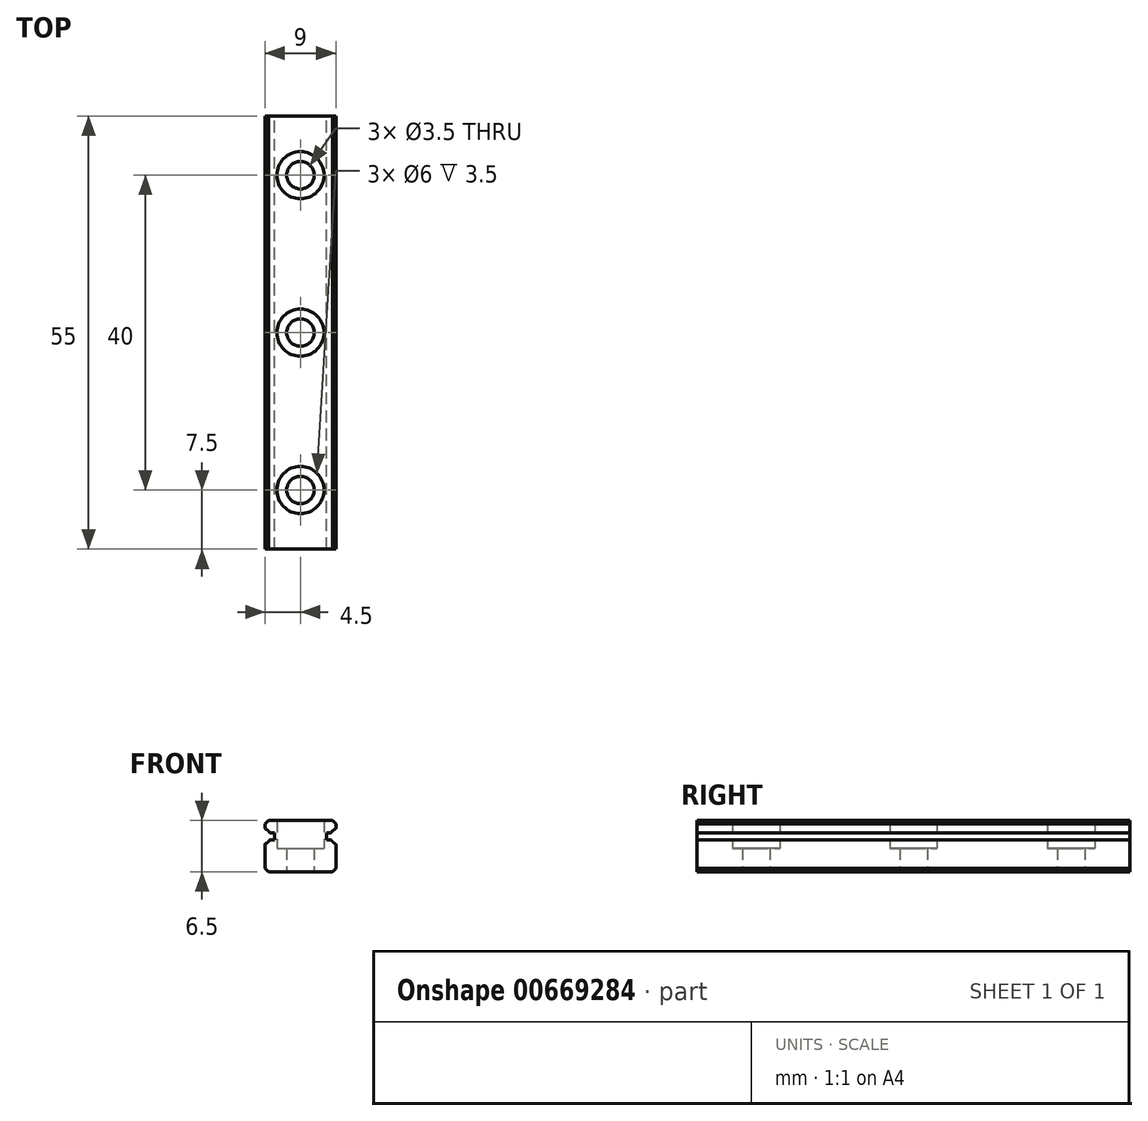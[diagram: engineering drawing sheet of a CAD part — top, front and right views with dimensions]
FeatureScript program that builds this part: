
annotation { "Feature Type Name" : "Feature", "Feature Type Description" : "" }
export const myFeature = defineFeature(function(context is Context, id is Id, definition is map)
    precondition{}
    {
        {
            var Q0;
            Q0=qCreatedBy(makeId("Front.planeOp"),FACE);
            var sketch = newSketch(context, id + "F0", { "sketchPlane" : qUnion([Q0])});
            skPoint(sketch, "E0.middle", {"position": v(0, 0) * mm});
            skLineSegment(sketch, "E1.bottom", {"start": v(0, -3.25) * mm, "end": v(-4.08, -3.25) * mm});
            skLineSegment(sketch, "E1.top", {"start": v(0, 3.25) * mm, "end": v(-4.08, 3.25) * mm});
            skLineSegment(sketch, "E1.right", {"start": v(-4.5, -2.83) * mm, "end": v(-4.5, 0.16) * mm});
            skArc(sketch, "E2", {"start": v(-4.38, 0.34) * mm, "mid": v(-4.15, 0.5) * mm, "end": v(-3.96, 0.7) * mm});
            skLineSegment(sketch, "E3", {"start": v(-3.3, 0.8) * mm, "end": v(-3.8, 0.8) * mm});
            skLineSegment(sketch, "E4", {"start": v(-3.3, 1.7) * mm, "end": v(-3.8, 1.7) * mm});
            skLineSegment(sketch, "E5", {"start": v(-4.5, 2.83) * mm, "end": v(-4.08, 3.25) * mm});
            skLineSegment(sketch, "E6.MirrorCS", {"start": v(-4.5, -2.83) * mm, "end": v(-4.08, -3.25) * mm});
            skPoint(sketch, "E7.orphan", {"position": v(-4.5, 3.25) * mm});
            skLineSegment(sketch, "E8.trimOffspring", {"start": v(-4.5, 2.34) * mm, "end": v(-4.5, 2.83) * mm});
            skArc(sketch, "E9.trimOffspring", {"start": v(-3.96, 1.8) * mm, "mid": v(-4.15, 2) * mm, "end": v(-4.38, 2.16) * mm});
            skPoint(sketch, "E10.orphan", {"position": v(-4.5, -3.25) * mm});
            skLineSegment(sketch, "E11", {"start": v(-3.3, 1.7) * mm, "end": v(-3.3, 0.8) * mm});
            skLineSegment(sketch, "E12", {"start": v(-4.8, 1.25) * mm, "end": v(0, 1.25) * mm, "construction": true});
            skLineSegment(sketch, "E13", {"start": v(0, 3.25) * mm, "end": v(0, -3.25) * mm, "construction": true});
            skPoint(sketch, "E14.0.visualSharp", {"position": v(-4.5, 0.3) * mm});
            skArc(sketch, "E14.0.filletArc", {"start": v(-4.38, 0.34) * mm, "mid": v(-4.47, 0.27) * mm, "end": v(-4.5, 0.16) * mm});
            skPoint(sketch, "E14.1.visualSharp", {"position": v(-3.9, 0.8) * mm});
            skArc(sketch, "E14.1.filletArc", {"start": v(-3.8, 0.8) * mm, "mid": v(-3.89, 0.78) * mm, "end": v(-3.96, 0.7) * mm});
            skPoint(sketch, "E14.2.visualSharp", {"position": v(-3.9, 1.7) * mm});
            skArc(sketch, "E14.2.filletArc", {"start": v(-3.96, 1.8) * mm, "mid": v(-3.89, 1.72) * mm, "end": v(-3.8, 1.7) * mm});
            skPoint(sketch, "E14.3.visualSharp", {"position": v(-4.5, 2.2) * mm});
            skArc(sketch, "E14.3.filletArc", {"start": v(-4.5, 2.34) * mm, "mid": v(-4.47, 2.23) * mm, "end": v(-4.38, 2.16) * mm});
            skLineSegment(sketch, "E15.MirrorCS", {"start": v(0, 3.25) * mm, "end": v(4.08, 3.25) * mm});
            skLineSegment(sketch, "E16.MirrorCS", {"start": v(4.5, 2.83) * mm, "end": v(4.08, 3.25) * mm});
            skLineSegment(sketch, "E17.MirrorCS", {"start": v(4.5, 2.34) * mm, "end": v(4.5, 2.83) * mm});
            skArc(sketch, "E18.MirrorCS", {"start": v(4.5, 2.34) * mm, "mid": v(4.47, 2.23) * mm, "end": v(4.38, 2.16) * mm});
            skArc(sketch, "E19.MirrorCS", {"start": v(3.96, 1.8) * mm, "mid": v(4.15, 2) * mm, "end": v(4.38, 2.16) * mm});
            skArc(sketch, "E20.MirrorCS", {"start": v(3.96, 1.8) * mm, "mid": v(3.89, 1.72) * mm, "end": v(3.8, 1.7) * mm});
            skLineSegment(sketch, "E21.MirrorCS", {"start": v(3.3, 1.7) * mm, "end": v(3.8, 1.7) * mm});
            skLineSegment(sketch, "E22.MirrorCS", {"start": v(3.3, 1.7) * mm, "end": v(3.3, 0.8) * mm});
            skLineSegment(sketch, "E23.MirrorCS", {"start": v(3.3, 0.8) * mm, "end": v(3.8, 0.8) * mm});
            skArc(sketch, "E24.MirrorCS", {"start": v(3.8, 0.8) * mm, "mid": v(3.89, 0.78) * mm, "end": v(3.96, 0.7) * mm});
            skArc(sketch, "E25.MirrorCS", {"start": v(4.38, 0.34) * mm, "mid": v(4.15, 0.5) * mm, "end": v(3.96, 0.7) * mm});
            skArc(sketch, "E26.MirrorCS", {"start": v(4.38, 0.34) * mm, "mid": v(4.47, 0.27) * mm, "end": v(4.5, 0.16) * mm});
            skLineSegment(sketch, "E27.MirrorCS", {"start": v(4.5, -2.83) * mm, "end": v(4.5, 0.16) * mm});
            skLineSegment(sketch, "E28.MirrorCS", {"start": v(4.5, -2.83) * mm, "end": v(4.08, -3.25) * mm});
            skLineSegment(sketch, "E29.MirrorCS", {"start": v(0, -3.25) * mm, "end": v(4.08, -3.25) * mm});
            skSolve(sketch);
        }
        {
            var Q0;
            Q0=makeQuery(id+"F0.imprint","IMPRINT",FACE,{"disambiguationData":[TD([[makeQuery(id+"F0.imprint","IMPRINT",EDGE,{"derivedFrom":sQuery(id+"F0.wireOp",EDGE,"E1.bottom")}),-1.0]])]});
            extrude(context, id + "F1", {"entities" : qUnion([Q0]), "depth" : 55 * mm, "offsetDistance" : 25 * mm});
        }
        {
            var Q0;
            Q0=makeQuery(id+"F1.opExtrude","SWEPT_FACE",FACE,{"disambiguationData":[OSD([sQuery(id+"F0.wireOp",EDGE,"E1.top")])]});
            var sketch = newSketch(context, id + "F2", { "sketchPlane" : qUnion([Q0])});
            skPoint(sketch, "E30", {"position": v(0, -7.5) * mm});
            skPoint(sketch, "E31.1.0.0", {"position": v(0, -27.5) * mm});
            skPoint(sketch, "E31.2.0.0", {"position": v(0, -47.5) * mm});
            skPoint(sketch, "E31.3.0.0", {"position": v(0, -67.5) * mm});
            skPoint(sketch, "E31.4.0.0", {"position": v(0, -87.5) * mm});
            skPoint(sketch, "E31.5.0.0", {"position": v(0, -107.5) * mm});
            skPoint(sketch, "E31.6.0.0", {"position": v(0, -127.5) * mm});
            skPoint(sketch, "E31.7.0.0", {"position": v(0, -147.5) * mm});
            skPoint(sketch, "E31.8.0.0", {"position": v(0, -167.5) * mm});
            skPoint(sketch, "E31.9.0.0", {"position": v(0, -187.5) * mm});
            skPoint(sketch, "E31.10.0.0", {"position": v(0, -207.5) * mm});
            skPoint(sketch, "E31.11.0.0", {"position": v(0, -227.5) * mm});
            skPoint(sketch, "E31.12.0.0", {"position": v(0, -247.5) * mm});
            skPoint(sketch, "E31.13.0.0", {"position": v(0, -267.5) * mm});
            skPoint(sketch, "E31.14.0.0", {"position": v(0, -287.5) * mm});
            skPoint(sketch, "E31.15.0.0", {"position": v(0, -307.5) * mm});
            skPoint(sketch, "E31.16.0.0", {"position": v(0, -327.5) * mm});
            skPoint(sketch, "E31.17.0.0", {"position": v(0, -347.5) * mm});
            skPoint(sketch, "E31.18.0.0", {"position": v(0, -367.5) * mm});
            skPoint(sketch, "E31.19.0.0", {"position": v(0, -387.5) * mm});
            skPoint(sketch, "E31.20.0.0", {"position": v(0, -407.5) * mm});
            skPoint(sketch, "E31.21.0.0", {"position": v(0, -427.5) * mm});
            skPoint(sketch, "E31.22.0.0", {"position": v(0, -447.5) * mm});
            skPoint(sketch, "E31.23.0.0", {"position": v(0, -467.5) * mm});
            skPoint(sketch, "E31.24.0.0", {"position": v(0, -487.5) * mm});
            skPoint(sketch, "E31.25.0.0", {"position": v(0, -507.5) * mm});
            skPoint(sketch, "E31.26.0.0", {"position": v(0, -527.5) * mm});
            skPoint(sketch, "E31.27.0.0", {"position": v(0, -547.5) * mm});
            skPoint(sketch, "E31.28.0.0", {"position": v(0, -567.5) * mm});
            skPoint(sketch, "E31.29.0.0", {"position": v(0, -587.5) * mm});
            skLineSegment(sketch, "E31.direction1", {"start": v(0, -7.5) * mm, "end": v(0, -27.5) * mm, "construction": true});
            skPoint(sketch, "E32.0.30.0", {"position": v(0, -607.5) * mm});
            skPoint(sketch, "E32.0.31.0", {"position": v(0, -627.5) * mm});
            skPoint(sketch, "E32.0.32.0", {"position": v(0, -647.5) * mm});
            skPoint(sketch, "E32.0.33.0", {"position": v(0, -667.5) * mm});
            skPoint(sketch, "E32.0.34.0", {"position": v(0, -687.5) * mm});
            skPoint(sketch, "E32.0.35.0", {"position": v(0, -707.5) * mm});
            skPoint(sketch, "E32.0.36.0", {"position": v(0, -727.5) * mm});
            skPoint(sketch, "E32.0.37.0", {"position": v(0, -747.5) * mm});
            skPoint(sketch, "E32.0.38.0", {"position": v(0, -767.5) * mm});
            skPoint(sketch, "E32.0.39.0", {"position": v(0, -787.5) * mm});
            skPoint(sketch, "E33.0.40.0", {"position": v(0, -807.5) * mm});
            skPoint(sketch, "E33.0.41.0", {"position": v(0, -827.5) * mm});
            skPoint(sketch, "E33.0.42.0", {"position": v(0, -847.5) * mm});
            skPoint(sketch, "E33.0.43.0", {"position": v(0, -867.5) * mm});
            skPoint(sketch, "E33.0.44.0", {"position": v(0, -887.5) * mm});
            skPoint(sketch, "E33.0.45.0", {"position": v(0, -907.5) * mm});
            skPoint(sketch, "E33.0.46.0", {"position": v(0, -927.5) * mm});
            skPoint(sketch, "E33.0.47.0", {"position": v(0, -947.5) * mm});
            skPoint(sketch, "E33.0.48.0", {"position": v(0, -967.5) * mm});
            skPoint(sketch, "E33.0.49.0", {"position": v(0, -987.5) * mm});
            skPoint(sketch, "E34.0.50.0", {"position": v(0, -1007.5) * mm});
            skPoint(sketch, "E34.0.51.0", {"position": v(0, -1027.5) * mm});
            skPoint(sketch, "E34.0.52.0", {"position": v(0, -1047.5) * mm});
            skPoint(sketch, "E34.0.53.0", {"position": v(0, -1067.5) * mm});
            skPoint(sketch, "E34.0.54.0", {"position": v(0, -1087.5) * mm});
            skPoint(sketch, "E34.0.55.0", {"position": v(0, -1107.5) * mm});
            skPoint(sketch, "E34.0.56.0", {"position": v(0, -1127.5) * mm});
            skPoint(sketch, "E34.0.57.0", {"position": v(0, -1147.5) * mm});
            skPoint(sketch, "E34.0.58.0", {"position": v(0, -1167.5) * mm});
            skPoint(sketch, "E34.0.59.0", {"position": v(0, -1187.5) * mm});
            skSolve(sketch);
        }
        {
            var Q0;
            Q0=sQuery(id+"F2.wireOp",VERTEX,"E34.0.52.0");
            var Q1;
            Q1=sQuery(id+"F2.wireOp",VERTEX,"E30");
            var Q2;
            Q2=sQuery(id+"F2.wireOp",VERTEX,"E34.0.59.0");
            var Q3;
            Q3=sQuery(id+"F2.wireOp",VERTEX,"E31.25.0.0");
            var Q4;
            Q4=sQuery(id+"F2.wireOp",VERTEX,"E34.0.50.0");
            var Q5;
            Q5=sQuery(id+"F2.wireOp",VERTEX,"E31.3.0.0");
            var Q6;
            Q6=sQuery(id+"F2.wireOp",VERTEX,"E33.0.40.0");
            var Q7;
            Q7=sQuery(id+"F2.wireOp",VERTEX,"E32.0.30.0");
            var Q8;
            Q8=sQuery(id+"F2.wireOp",VERTEX,"E32.0.33.0");
            var Q9;
            Q9=sQuery(id+"F2.wireOp",VERTEX,"E31.direction1.end");
            var Q10;
            Q10=sQuery(id+"F2.wireOp",VERTEX,"E31.24.0.0");
            var Q11;
            Q11=sQuery(id+"F2.wireOp",VERTEX,"E31.9.0.0");
            var Q12;
            Q12=sQuery(id+"F2.wireOp",VERTEX,"E31.19.0.0");
            var Q13;
            Q13=sQuery(id+"F2.wireOp",VERTEX,"E31.23.0.0");
            var Q14;
            Q14=sQuery(id+"F2.wireOp",VERTEX,"E33.0.47.0");
            var Q15;
            Q15=sQuery(id+"F2.wireOp",VERTEX,"E31.4.0.0");
            var Q16;
            Q16=sQuery(id+"F2.wireOp",VERTEX,"E31.20.0.0");
            var Q17;
            Q17=sQuery(id+"F2.wireOp",VERTEX,"E31.11.0.0");
            var Q18;
            Q18=sQuery(id+"F2.wireOp",VERTEX,"E32.0.32.0");
            var Q19;
            Q19=sQuery(id+"F2.wireOp",VERTEX,"E32.0.39.0");
            var Q20;
            Q20=sQuery(id+"F2.wireOp",VERTEX,"E32.0.36.0");
            var Q21;
            Q21=sQuery(id+"F2.wireOp",VERTEX,"E32.0.37.0");
            var Q22;
            Q22=sQuery(id+"F2.wireOp",VERTEX,"E33.0.49.0");
            var Q23;
            Q23=sQuery(id+"F2.wireOp",VERTEX,"E32.0.38.0");
            var Q24;
            Q24=sQuery(id+"F2.wireOp",VERTEX,"E34.0.56.0");
            var Q25;
            Q25=sQuery(id+"F2.wireOp",VERTEX,"E33.0.44.0");
            var Q26;
            Q26=sQuery(id+"F2.wireOp",VERTEX,"E31.10.0.0");
            var Q27;
            Q27=sQuery(id+"F2.wireOp",VERTEX,"E31.28.0.0");
            var Q28;
            Q28=sQuery(id+"F2.wireOp",VERTEX,"E34.0.55.0");
            var Q29;
            Q29=sQuery(id+"F2.wireOp",VERTEX,"E32.0.35.0");
            var Q30;
            Q30=sQuery(id+"F2.wireOp",VERTEX,"E34.0.51.0");
            var Q31;
            Q31=sQuery(id+"F2.wireOp",VERTEX,"E31.13.0.0");
            var Q32;
            Q32=sQuery(id+"F2.wireOp",VERTEX,"E31.2.0.0");
            var Q33;
            Q33=sQuery(id+"F2.wireOp",VERTEX,"E31.21.0.0");
            var Q34;
            Q34=sQuery(id+"F2.wireOp",VERTEX,"E32.0.34.0");
            var Q35;
            Q35=sQuery(id+"F2.wireOp",VERTEX,"E31.16.0.0");
            var Q36;
            Q36=sQuery(id+"F2.wireOp",VERTEX,"E31.7.0.0");
            var Q37;
            Q37=sQuery(id+"F2.wireOp",VERTEX,"E32.0.31.0");
            var Q38;
            Q38=sQuery(id+"F2.wireOp",VERTEX,"E31.8.0.0");
            var Q39;
            Q39=sQuery(id+"F2.wireOp",VERTEX,"E34.0.57.0");
            var Q40;
            Q40=sQuery(id+"F2.wireOp",VERTEX,"E31.17.0.0");
            var Q41;
            Q41=sQuery(id+"F2.wireOp",VERTEX,"E31.12.0.0");
            var Q42;
            Q42=sQuery(id+"F2.wireOp",VERTEX,"E33.0.48.0");
            var Q43;
            Q43=sQuery(id+"F2.wireOp",VERTEX,"E31.18.0.0");
            var Q44;
            Q44=sQuery(id+"F2.wireOp",VERTEX,"E31.15.0.0");
            var Q45;
            Q45=sQuery(id+"F2.wireOp",VERTEX,"E34.0.54.0");
            var Q46;
            Q46=sQuery(id+"F2.wireOp",VERTEX,"E34.0.58.0");
            var Q47;
            Q47=sQuery(id+"F2.wireOp",VERTEX,"E33.0.46.0");
            var Q48;
            Q48=sQuery(id+"F2.wireOp",VERTEX,"E31.22.0.0");
            var Q49;
            Q49=sQuery(id+"F2.wireOp",VERTEX,"E31.14.0.0");
            var Q50;
            Q50=sQuery(id+"F2.wireOp",VERTEX,"E31.29.0.0");
            var Q51;
            Q51=sQuery(id+"F2.wireOp",VERTEX,"E33.0.45.0");
            var Q52;
            Q52=sQuery(id+"F2.wireOp",VERTEX,"E31.6.0.0");
            var Q53;
            Q53=sQuery(id+"F2.wireOp",VERTEX,"E33.0.42.0");
            var Q54;
            Q54=sQuery(id+"F2.wireOp",VERTEX,"E31.5.0.0");
            var Q55;
            Q55=sQuery(id+"F2.wireOp",VERTEX,"E31.26.0.0");
            var Q56;
            Q56=sQuery(id+"F2.wireOp",VERTEX,"E33.0.41.0");
            var Q57;
            Q57=sQuery(id+"F2.wireOp",VERTEX,"E34.0.53.0");
            var Q58;
            Q58=sQuery(id+"F2.wireOp",VERTEX,"E33.0.43.0");
            var Q59;
            Q59=sQuery(id+"F2.wireOp",VERTEX,"E31.27.0.0");
            var Q60;
            Q60=makeQuery(id+"F1.opExtrude","SWEPT_BODY",BODY,{"disambiguationData":[OSD([sQuery(id+"F0.wireOp",EDGE,"E1.bottom"),sQuery(id+"F0.wireOp",EDGE,"E1.top"),sQuery(id+"F0.wireOp",EDGE,"E1.left"),sQuery(id+"F0.wireOp",EDGE,"E1.right"),sQuery(id+"F0.wireOp",EDGE,"E2"),sQuery(id+"F0.wireOp",EDGE,"6b0fc32b-6b11-43fe-8143-8292133b5b09"),sQuery(id+"F0.wireOp",EDGE,"cceb31f5-90f8-4f8b-8e4c-378b10a37ca3"),sQuery(id+"F0.wireOp",EDGE,"a502a9f8-cd79-42af-b1f8-1e47760ff194"),sQuery(id+"F0.wireOp",EDGE,"E3"),sQuery(id+"F0.wireOp",EDGE,"E4"),sQuery(id+"F0.wireOp",EDGE,"E5"),sQuery(id+"F0.wireOp",EDGE,"f517c70c-7447-4023-b0b2-4cd41b919897.MirrorCS"),sQuery(id+"F0.wireOp",EDGE,"1ef16270-10e6-46b5-932e-9d39ff3028f5.MirrorCS"),sQuery(id+"F0.wireOp",EDGE,"E6.MirrorCS"),sQuery(id+"F0.wireOp",EDGE,"E8.trimOffspring"),sQuery(id+"F0.wireOp",EDGE,"E9.trimOffspring"),sQuery(id+"F0.wireOp",EDGE,"67894982-00cf-4a8e-9807-128cd8b838d2.trimOffspring"),sQuery(id+"F0.wireOp",EDGE,"f8798748-f2cf-45fa-b449-962a41418a19.trimOffspring"),sQuery(id+"F0.wireOp",EDGE,"E11"),sQuery(id+"F0.wireOp",EDGE,"PUignqLn-Sdhw-Ye5u-4mVw-quTeRiMXk1mG")])]});
            hole(context, id + "F3", {"style" : HoleStyle.C_BORE, "endStyle" : HoleEndStyle.THROUGH, "holeDiameter" : 3.5 * mm, "cBoreDiameter" : 6 * mm, "cBoreDepth" : 3.5 * mm, "majorDiameter" : 5 * mm, "isTappedThrough" : true, "tappedDepth" : 12 * mm, "tapClearance" : 3, "locations" : qUnion([Q0, Q1, Q2, Q3, Q4, Q5, Q6, Q7, Q8, Q9, Q10, Q11, Q12, Q13, Q14, Q15, Q16, Q17, Q18, Q19, Q20, Q21, Q22, Q23, Q24, Q25, Q26, Q27, Q28, Q29, Q30, Q31, Q32, Q33, Q34, Q35, Q36, Q37, Q38, Q39, Q40, Q41, Q42, Q43, Q44, Q45, Q46, Q47, Q48, Q49, Q50, Q51, Q52, Q53, Q54, Q55, Q56, Q57, Q58, Q59]), "scope" : qUnion([Q60]), "startStyle" : HoleStartStyle.PART});
        }
    });
